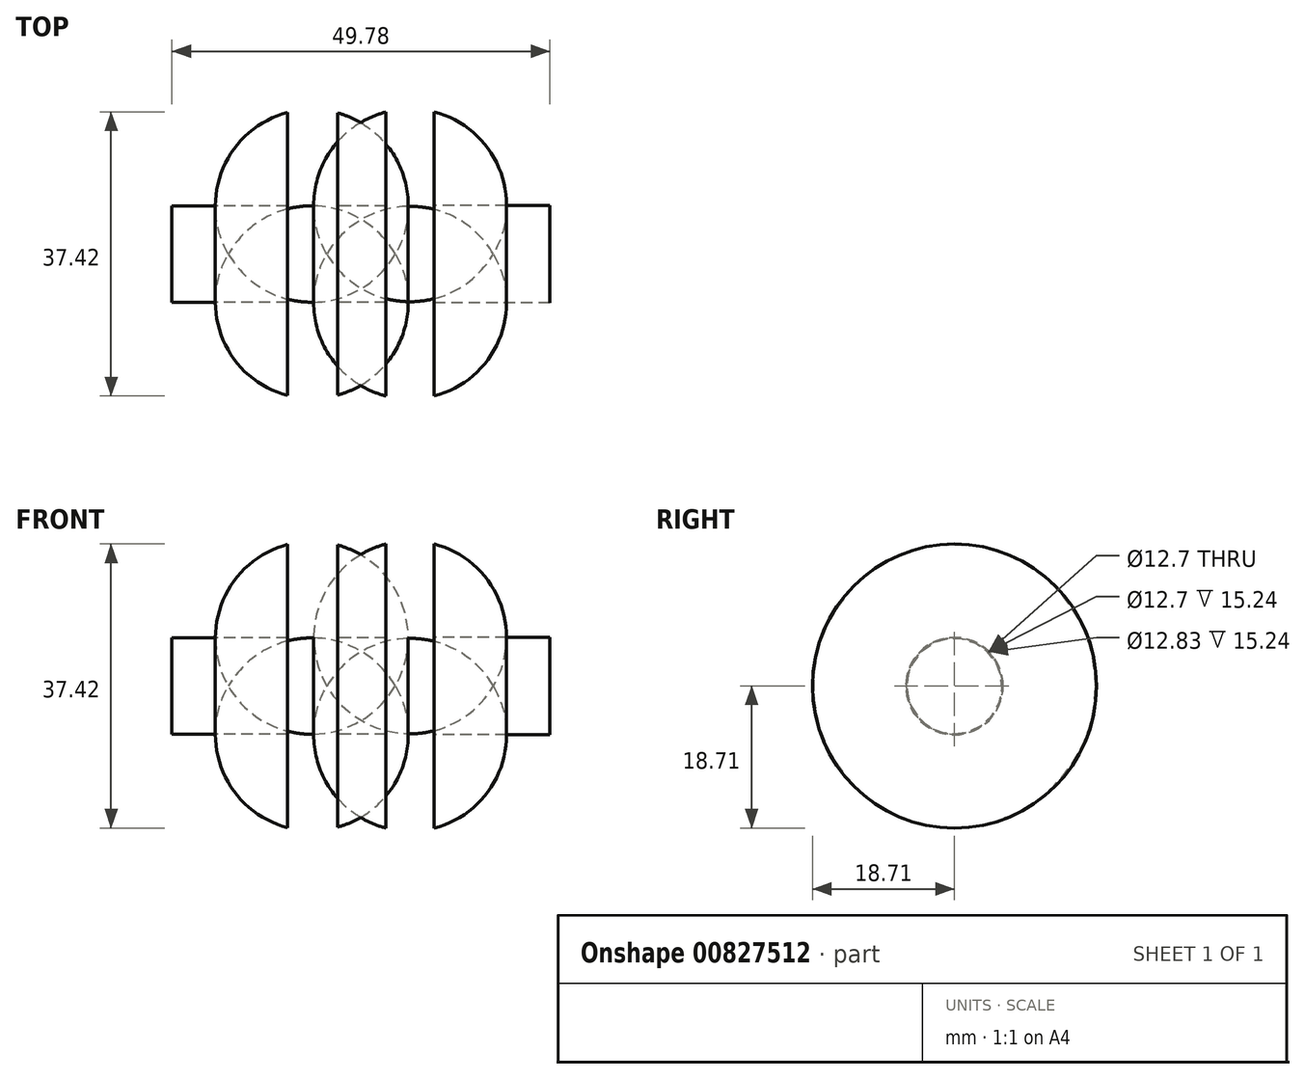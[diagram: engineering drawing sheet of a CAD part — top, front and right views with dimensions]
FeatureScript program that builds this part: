
annotation { "Feature Type Name" : "Feature", "Feature Type Description" : "" }
export const myFeature = defineFeature(function(context is Context, id is Id, definition is map)
    precondition{}
    {
        {
            var Q0;
            Q0=qCreatedBy(makeId("Top.planeOp"),FACE);
            var sketch = newSketch(context, id + "F0", { "sketchPlane" : qUnion([Q0])});
            skLineSegment(sketch, "E0", {"start": v(-3.18, 18.65) * mm, "end": v(-3.18, 6.35) * mm});
            skLineSegment(sketch, "E1", {"start": v(3.42, 6.35) * mm, "end": v(3.42, 18.58) * mm});
            skPoint(sketch, "E2.orphan", {"position": v(3.42, 21.27) * mm});
            skPoint(sketch, "E3.orphan", {"position": v(-3.18, 21.27) * mm});
            skArc(sketch, "E4.trimOffspring", {"start": v(3.42, 18.58) * mm, "mid": v(0.13, 19.05) * mm, "end": v(-3.17, 18.65) * mm});
            skPoint(sketch, "E5.orphan", {"position": v(-3.17, -14.98) * mm});
            skLineSegment(sketch, "E6", {"start": v(-3.18, 6.35) * mm, "end": v(-18.41, 6.35) * mm});
            skLineSegment(sketch, "E7", {"start": v(-18.41, 6.35) * mm, "end": v(-18.41, 0) * mm});
            skLineSegment(sketch, "E8", {"start": v(3.42, 6.35) * mm, "end": v(9.77, 6.35) * mm});
            skLineSegment(sketch, "E9", {"start": v(9.77, 18.71) * mm, "end": v(9.77, 6.35) * mm});
            skLineSegment(sketch, "E10", {"start": v(16.12, 6.41) * mm, "end": v(16.12, 18.71) * mm});
            skArc(sketch, "E11.trimOffspring", {"start": v(16.12, 18.71) * mm, "mid": v(12.94, 19.11) * mm, "end": v(9.77, 18.71) * mm});
            skLineSegment(sketch, "E12", {"start": v(16.12, 6.41) * mm, "end": v(31.36, 6.41) * mm});
            skLineSegment(sketch, "E13", {"start": v(31.36, 6.41) * mm, "end": v(31.36, 0) * mm});
            skPoint(sketch, "E14.end.orphan", {"position": v(3.42, -5.88) * mm});
            skPoint(sketch, "E14.start.orphan", {"position": v(-3.17, -5.95) * mm});
            skPoint(sketch, "E15.end.orphan", {"position": v(16.12, -5.88) * mm});
            skLineSegment(sketch, "E16", {"start": v(-24.03, 0) * mm, "end": v(36.2, 0) * mm, "construction": true});
            skLineSegment(sketch, "E17", {"start": v(-18.41, 0) * mm, "end": v(31.36, 0) * mm});
            skSolve(sketch);
        }
        {
            var Q0;
            Q0=makeQuery(id+"F0.imprint","IMPRINT",FACE,{"disambiguationData":[TD([[makeQuery(id+"F0.imprint","IMPRINT",EDGE,{"derivedFrom":sQuery(id+"F0.wireOp",EDGE,"E0")}),1.0]])]});
            var Q1;
            Q1=sQuery(id+"F0.wireOp",EDGE,"E16");
            revolve(context, id + "F1", {"surfaceOperationType" : NewSurfaceOperationType.NEW, "entities" : qUnion([Q0]), "axis" : qUnion([Q1]), "revolveType" : RevolveType.FULL});
        }
    });
